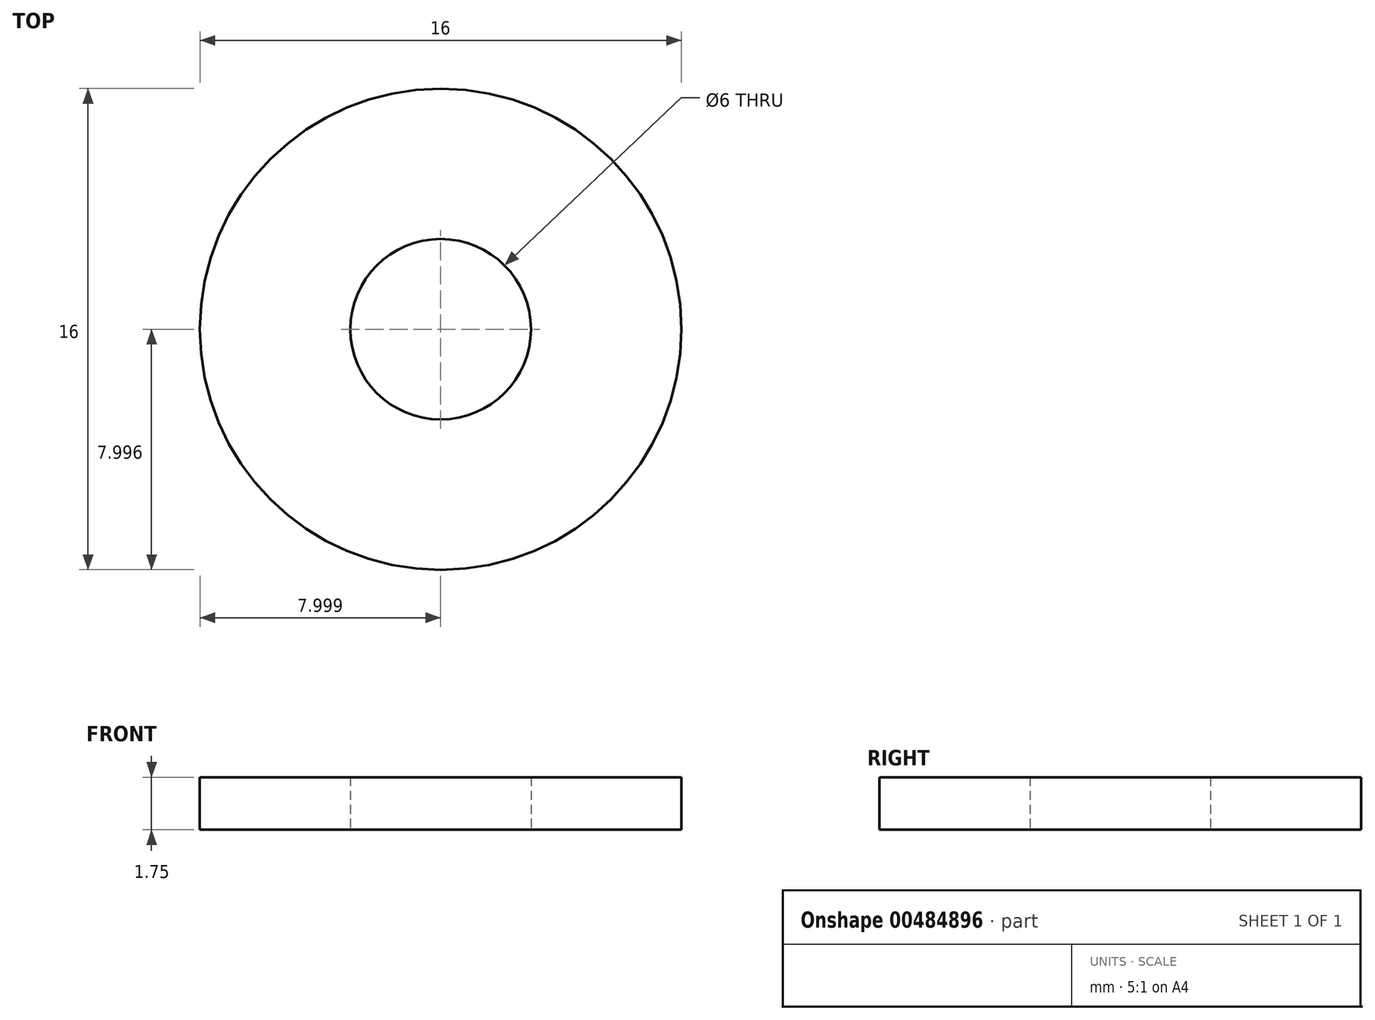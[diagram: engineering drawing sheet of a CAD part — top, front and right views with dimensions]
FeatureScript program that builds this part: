
annotation { "Feature Type Name" : "Feature", "Feature Type Description" : "" }
export const myFeature = defineFeature(function(context is Context, id is Id, definition is map)
    precondition{}
    {
        {
            var Q0;
            Q0=qCreatedBy(makeId("Top.planeOp"),FACE);
            var sketch = newSketch(context, id + "F0", { "sketchPlane" : qUnion([Q0])});
            skCircle(sketch, "E0", {"center": v(-14.18, 15.17) * mm, "radius": 8 * mm});
            skCircle(sketch, "E1", {"center": v(-14.18, 15.17) * mm, "radius": 3 * mm});
            skSolve(sketch);
        }
        {
            var Q0;
            Q0=makeQuery(id+"F0.imprint","IMPRINT",FACE,{"disambiguationData":[TD([[makeQuery(id+"F0.imprint","IMPRINT",EDGE,{"derivedFrom":sQuery(id+"F0.wireOp",EDGE,"E0")}),1.0]])]});
            extrude(context, id + "F1", {"entities" : qUnion([Q0]), "depth" : 1.75 * mm});
        }
    });
